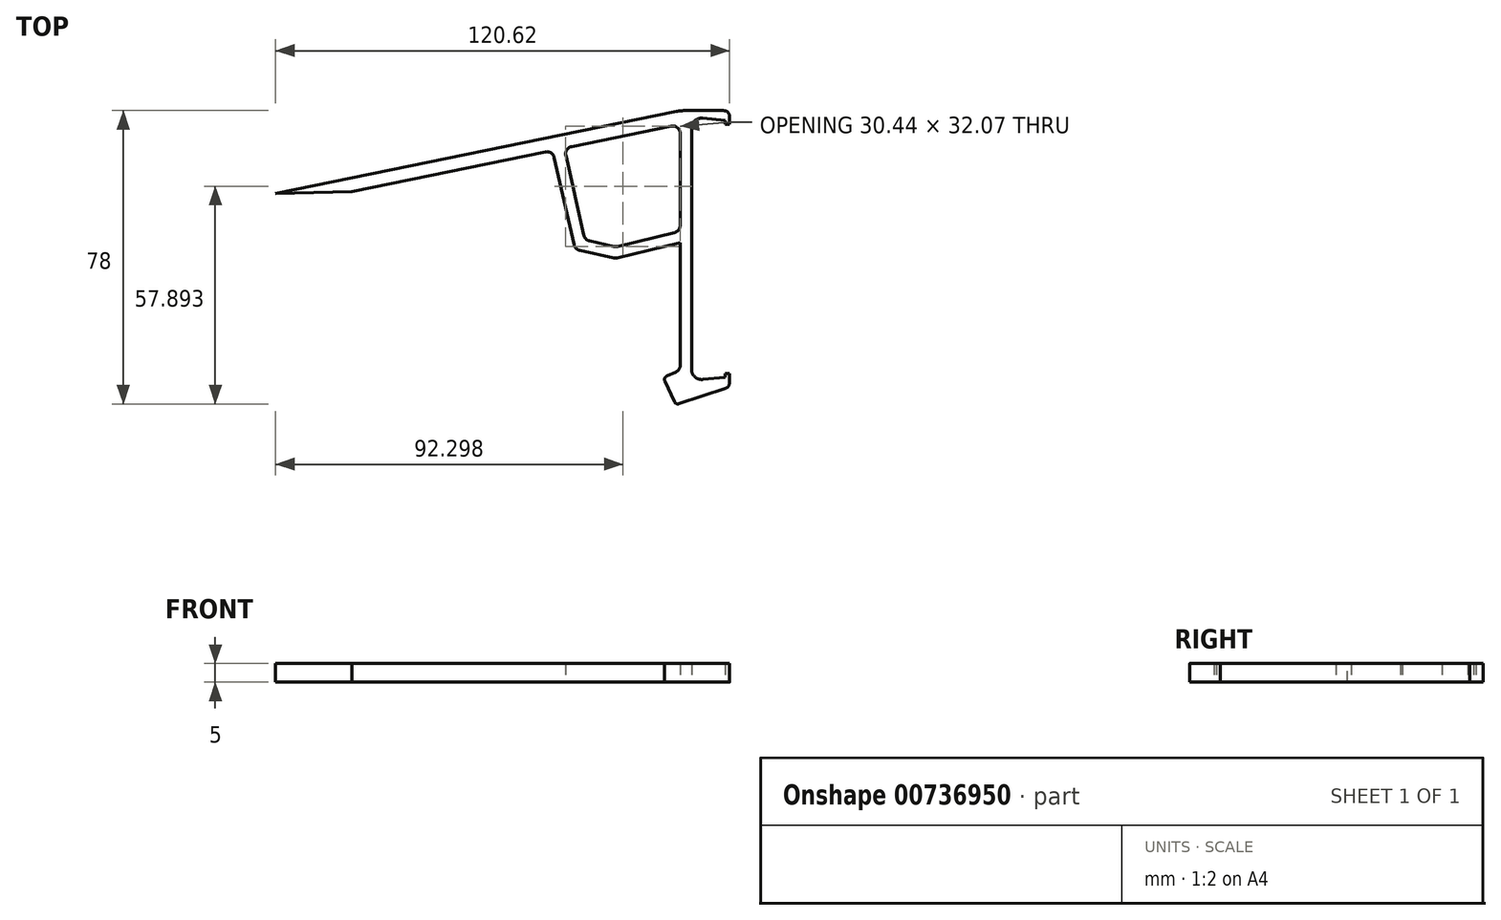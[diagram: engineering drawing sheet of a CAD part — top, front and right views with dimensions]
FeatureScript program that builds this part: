
annotation { "Feature Type Name" : "Feature", "Feature Type Description" : "" }
export const myFeature = defineFeature(function(context is Context, id is Id, definition is map)
    precondition{}
    {
        {
            var Q0;
            Q0=qCreatedBy(makeId("Top.planeOp"),FACE);
            var sketch = newSketch(context, id + "F0", { "sketchPlane" : qUnion([Q0])});
            skLineSegment(sketch, "E0.bottom", {"start": v(0, 69.5) * mm, "end": v(9, 69.5) * mm, "construction": true});
            skLineSegment(sketch, "E0.top", {"start": v(0, 0) * mm, "end": v(9, 0) * mm, "construction": true});
            skLineSegment(sketch, "E0.left", {"start": v(0, 69.5) * mm, "end": v(0, 0) * mm, "construction": true});
            skLineSegment(sketch, "E0.right", {"start": v(9, 69.5) * mm, "end": v(9, 0) * mm, "construction": true});
            skLineSegment(sketch, "E1", {"start": v(3, 0) * mm, "end": v(9, 0.6) * mm});
            skLineSegment(sketch, "E2", {"start": v(9, 34.75) * mm, "end": v(-49.16, 34.75) * mm, "construction": true});
            skArc(sketch, "E3", {"start": v(3, 0) * mm, "mid": v(0.9, 0.7) * mm, "end": v(0, 2.71) * mm});
            skLineSegment(sketch, "E4", {"start": v(9, 0.6) * mm, "end": v(8.9, 1.6) * mm});
            skLineSegment(sketch, "E5", {"start": v(8.9, 1.6) * mm, "end": v(10.1, 1.6) * mm});
            skLineSegment(sketch, "E6", {"start": v(10.1, 1.6) * mm, "end": v(10.1, -2) * mm});
            skLineSegment(sketch, "E7", {"start": v(10.1, -2) * mm, "end": v(-3, -2) * mm, "construction": true});
            skLineSegment(sketch, "E8.MirrorCS", {"start": v(9, 68.9) * mm, "end": v(8.9, 67.9) * mm});
            skLineSegment(sketch, "E9.MirrorCS", {"start": v(8.9, 67.9) * mm, "end": v(10.1, 67.9) * mm});
            skLineSegment(sketch, "E10.MirrorCS", {"start": v(3, 69.5) * mm, "end": v(9, 68.9) * mm});
            skLineSegment(sketch, "E11.MirrorCS", {"start": v(10.1, 71.5) * mm, "end": v(-3, 71.5) * mm});
            skArc(sketch, "E12.MirrorCS", {"start": v(3, 69.5) * mm, "mid": v(0.9, 68.8) * mm, "end": v(0, 66.79) * mm});
            skLineSegment(sketch, "E13.MirrorCS", {"start": v(10.1, 67.9) * mm, "end": v(10.1, 71.5) * mm});
            skLineSegment(sketch, "E14", {"start": v(0, 66.79) * mm, "end": v(0, 2.71) * mm});
            skLineSegment(sketch, "E15", {"start": v(-3, 67.88) * mm, "end": v(-3, 39.46) * mm, "construction": true});
            skLineSegment(sketch, "E16", {"start": v(10.1, -2) * mm, "end": v(-4.18, -6.73) * mm});
            skLineSegment(sketch, "E17", {"start": v(-4.18, -6.73) * mm, "end": v(-7.5, 0.49) * mm});
            skLineSegment(sketch, "E18", {"start": v(-7.5, 0.49) * mm, "end": v(-3, 2.55) * mm});
            skLineSegment(sketch, "E19", {"start": v(-3, 2.55) * mm, "end": v(-3, 36.4) * mm});
            skLineSegment(sketch, "E20", {"start": v(-3, 71.5) * mm, "end": v(-110.52, 49.46) * mm});
            skLineSegment(sketch, "E21", {"start": v(-110.52, 49.46) * mm, "end": v(-90.29, 49.99) * mm});
            skLineSegment(sketch, "E22", {"start": v(-90.29, 49.99) * mm, "end": v(-36.9, 60.93) * mm});
            skLineSegment(sketch, "E23", {"start": v(-3, 36.4) * mm, "end": v(-20.21, 32.22) * mm});
            skLineSegment(sketch, "E24", {"start": v(-20.21, 32.22) * mm, "end": v(-30.93, 34.6) * mm});
            skLineSegment(sketch, "E25", {"start": v(-30.93, 34.6) * mm, "end": v(-36.9, 60.93) * mm});
            skLineSegment(sketch, "E26", {"start": v(-33.85, 61.56) * mm, "end": v(-28.31, 37.12) * mm});
            skLineSegment(sketch, "E27", {"start": v(-28.31, 37.12) * mm, "end": v(-20.14, 35.3) * mm});
            skLineSegment(sketch, "E28", {"start": v(-20.14, 35.3) * mm, "end": v(-3, 39.46) * mm});
            skLineSegment(sketch, "E29.trimOffspring", {"start": v(-3, 36.4) * mm, "end": v(-3, -2) * mm, "construction": true});
            skLineSegment(sketch, "E30.trimOffspring", {"start": v(-3, 39.46) * mm, "end": v(-3, 67.88) * mm});
            skLineSegment(sketch, "E31.trimOffspring", {"start": v(-33.85, 61.56) * mm, "end": v(-3, 67.88) * mm});
            skSolve(sketch);
        }
        {
            var Q0;
            Q0=makeQuery(id+"F0.imprint","IMPRINT",FACE,{"disambiguationData":[TD([[makeQuery(id+"F0.imprint","IMPRINT",EDGE,{"derivedFrom":sQuery(id+"F0.wireOp",EDGE,"E1")}),-1.0]])]});
            extrude(context, id + "F1", {"entities" : qUnion([Q0]), "depth" : 5 * mm, "offsetDistance" : 25 * mm});
        }
        {
            var Q0;
            Q0=makeQuery(id+"F1.opExtrude","SWEPT_EDGE",EDGE,{"disambiguationData":[OSD([sQuery(id+"F0.wireOp",EDGE,"E13.MirrorCS"),sQuery(id+"F0.wireOp",EDGE,"E11.MirrorCS")])]});
            var Q1;
            Q1=makeQuery(id+"F1.opExtrude","SWEPT_EDGE",EDGE,{"disambiguationData":[OSD([sQuery(id+"F0.wireOp",EDGE,"E6"),sQuery(id+"F0.wireOp",EDGE,"E16")])]});
            fillet(context, id + "F2", {"entities" : qUnion([Q0, Q1]), "radius" : 1.5 * mm, "tangentPropagation" : true, "allowEdgeOverflow" : false});
        }
        {
            var Q0;
            Q0=makeQuery(id+"F1.opExtrude","SWEPT_EDGE",EDGE,{"disambiguationData":[OSD([sQuery(id+"F0.wireOp",EDGE,"E18"),sQuery(id+"F0.wireOp",EDGE,"E19")])]});
            var Q1;
            Q1=makeQuery(id+"F1.opExtrude","SWEPT_EDGE",EDGE,{"disambiguationData":[OSD([sQuery(id+"F0.wireOp",EDGE,"E28"),sQuery(id+"F0.wireOp",EDGE,"E30.trimOffspring")])]});
            var Q2;
            Q2=makeQuery(id+"F1.opExtrude","SWEPT_EDGE",EDGE,{"disambiguationData":[OSD([sQuery(id+"F0.wireOp",EDGE,"E27"),sQuery(id+"F0.wireOp",EDGE,"E28")])]});
            var Q3;
            Q3=makeQuery(id+"F1.opExtrude","SWEPT_EDGE",EDGE,{"disambiguationData":[OSD([sQuery(id+"F0.wireOp",EDGE,"E26"),sQuery(id+"F0.wireOp",EDGE,"E27")])]});
            var Q4;
            Q4=makeQuery(id+"F1.opExtrude","SWEPT_EDGE",EDGE,{"disambiguationData":[OSD([sQuery(id+"F0.wireOp",EDGE,"E26"),sQuery(id+"F0.wireOp",EDGE,"E31.trimOffspring")])]});
            var Q5;
            Q5=makeQuery(id+"F1.opExtrude","SWEPT_EDGE",EDGE,{"disambiguationData":[OSD([sQuery(id+"F0.wireOp",EDGE,"E30.trimOffspring"),sQuery(id+"F0.wireOp",EDGE,"E31.trimOffspring")])]});
            var Q6;
            Q6=makeQuery(id+"F1.opExtrude","SWEPT_EDGE",EDGE,{"disambiguationData":[OSD([sQuery(id+"F0.wireOp",EDGE,"E22"),sQuery(id+"F0.wireOp",EDGE,"E25")])]});
            var Q7;
            Q7=makeQuery(id+"F1.opExtrude","SWEPT_EDGE",EDGE,{"disambiguationData":[OSD([sQuery(id+"F0.wireOp",EDGE,"E24"),sQuery(id+"F0.wireOp",EDGE,"E25")])]});
            var Q8;
            Q8=makeQuery(id+"F1.opExtrude","SWEPT_EDGE",EDGE,{"disambiguationData":[OSD([sQuery(id+"F0.wireOp",EDGE,"E23"),sQuery(id+"F0.wireOp",EDGE,"E24")])]});
            fillet(context, id + "F3", {"entities" : qUnion([Q0, Q1, Q2, Q3, Q4, Q5, Q6, Q7, Q8]), "radius" : 2 * mm, "tangentPropagation" : true, "allowEdgeOverflow" : false});
        }
        {
            var Q0;
            Q0=makeQuery(id+"F1.opExtrude","SWEPT_EDGE",EDGE,{"disambiguationData":[OSD([sQuery(id+"F0.wireOp",EDGE,"E11.MirrorCS"),sQuery(id+"F0.wireOp",EDGE,"E20")])]});
            fillet(context, id + "F4", {"entities" : qUnion([Q0]), "radius" : 10 * mm, "tangentPropagation" : true, "allowEdgeOverflow" : false});
        }
        {
            var Q0;
            Q0=makeQuery(id+"F1.opExtrude","SWEPT_EDGE",EDGE,{"disambiguationData":[OSD([sQuery(id+"F0.wireOp",EDGE,"E16"),sQuery(id+"F0.wireOp",EDGE,"E17")])]});
            var Q1;
            Q1=makeQuery(id+"F1.opExtrude","SWEPT_EDGE",EDGE,{"disambiguationData":[OSD([sQuery(id+"F0.wireOp",EDGE,"E17"),sQuery(id+"F0.wireOp",EDGE,"E18")])]});
            fillet(context, id + "F5", {"entities" : qUnion([Q0, Q1]), "radius" : 1 * mm, "tangentPropagation" : true, "allowEdgeOverflow" : false});
        }
    });
